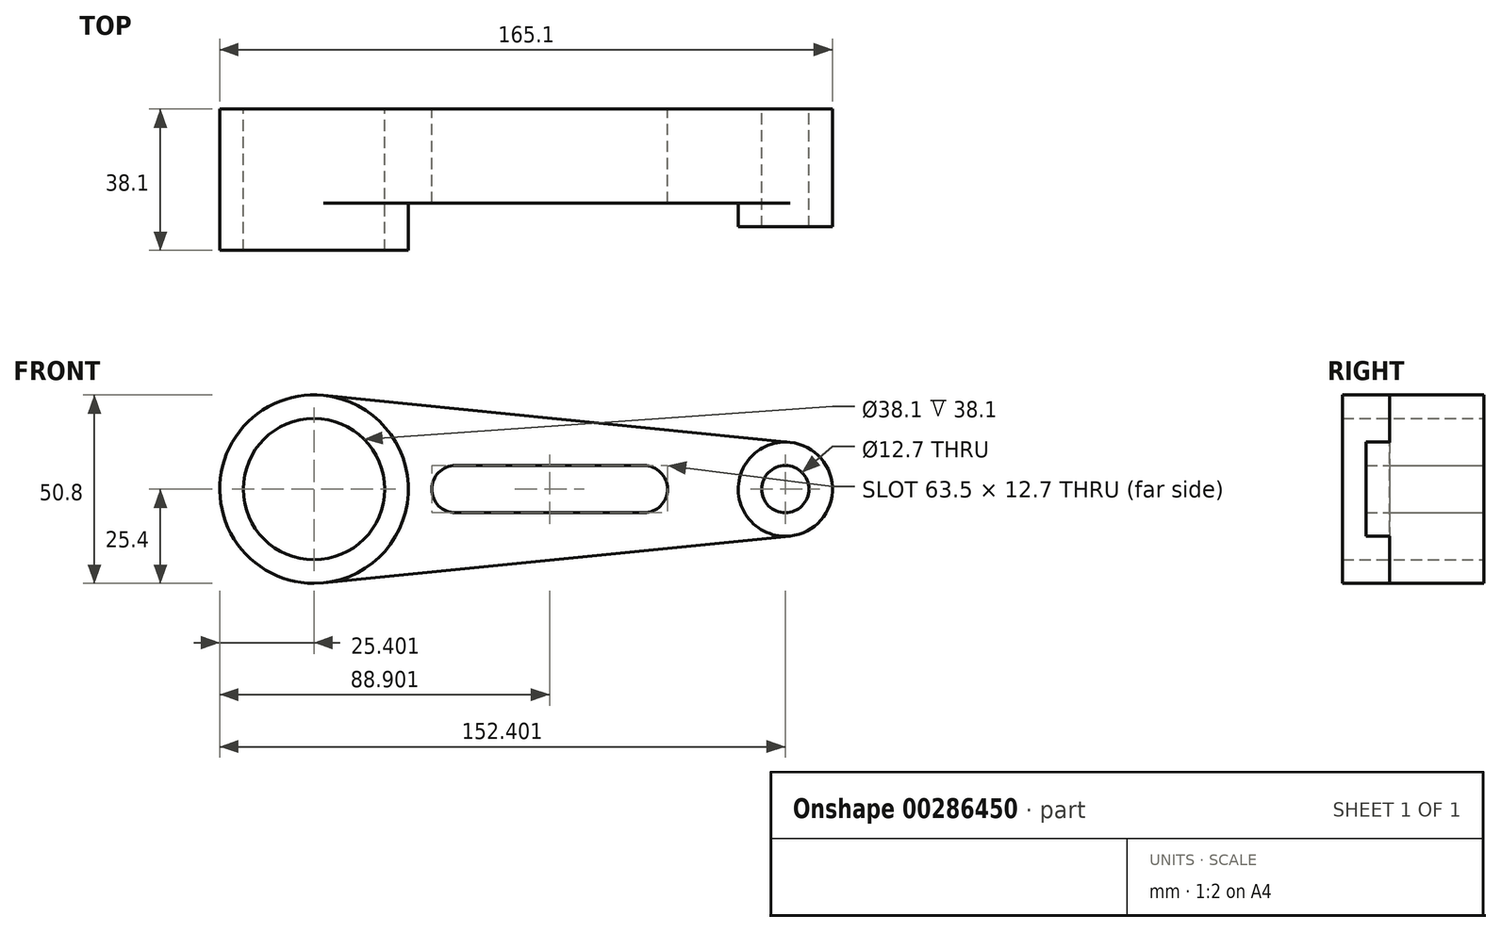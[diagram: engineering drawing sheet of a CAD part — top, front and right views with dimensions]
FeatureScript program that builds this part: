
annotation { "Feature Type Name" : "Feature", "Feature Type Description" : "" }
export const myFeature = defineFeature(function(context is Context, id is Id, definition is map)
    precondition{}
    {
        {
            var Q0;
            Q0=qCreatedBy(makeId("Front.planeOp"),FACE);
            var sketch = newSketch(context, id + "F0", { "sketchPlane" : qUnion([Q0])});
            skCircle(sketch, "E0", {"center": v(-80.1, 0) * mm, "radius": 25.4 * mm});
            skArc(sketch, "E1", {"start": v(-42, 6.35) * mm, "mid": v(-48.36, 0) * mm, "end": v(-42, -6.35) * mm});
            skArc(sketch, "E2", {"start": v(8.8, -6.35) * mm, "mid": v(15.14, 0) * mm, "end": v(8.8, 6.35) * mm});
            skCircle(sketch, "E3", {"center": v(-80.1, 0) * mm, "radius": 19.05 * mm});
            skCircle(sketch, "E4", {"center": v(46.9, 0) * mm, "radius": 12.7 * mm});
            skCircle(sketch, "E5", {"center": v(46.9, 0) * mm, "radius": 6.35 * mm});
            skLineSegment(sketch, "E6", {"start": v(-77.57, 25.27) * mm, "end": v(48.16, 12.64) * mm});
            skLineSegment(sketch, "E7", {"start": v(-77.57, -25.27) * mm, "end": v(48.16, -12.64) * mm});
            skLineSegment(sketch, "E8", {"start": v(-42, 6.35) * mm, "end": v(8.8, 6.35) * mm});
            skLineSegment(sketch, "E9", {"start": v(-42, -6.35) * mm, "end": v(8.8, -6.35) * mm});
            skSolve(sketch);
        }
        {
            var Q0;
            Q0=makeQuery(id+"F0.imprint","IMPRINT",FACE,{"disambiguationData":[TD([[makeQuery(id+"F0.imprint","IMPRINT",EDGE,{"derivedFrom":sQuery(id+"F0.wireOp",EDGE,"E3")}),-1.0]])]});
            extrude(context, id + "F1", {"entities" : qUnion([Q0]), "depth" : 38.1 * mm});
        }
        {
            var Q0;
            Q0=makeQuery(id+"F0.imprint","IMPRINT",FACE,{"disambiguationData":[TD([[makeQuery(id+"F0.imprint","IMPRINT",EDGE,{"derivedFrom":sQuery(id+"F0.wireOp",EDGE,"E1")}),-1.0]])]});
            extrude(context, id + "F2", {"entities" : qUnion([Q0]), "operationType" : NewBodyOperationType.ADD, "depth" : 25.4 * mm});
        }
        {
            var Q0;
            Q0=makeQuery(id+"F0.imprint","IMPRINT",FACE,{"disambiguationData":[TD([[makeQuery(id+"F0.imprint","IMPRINT",EDGE,{"derivedFrom":sQuery(id+"F0.wireOp",EDGE,"E5")}),-1.0]])]});
            extrude(context, id + "F3", {"entities" : qUnion([Q0]), "operationType" : NewBodyOperationType.ADD, "depth" : 31.75 * mm});
        }
    });
